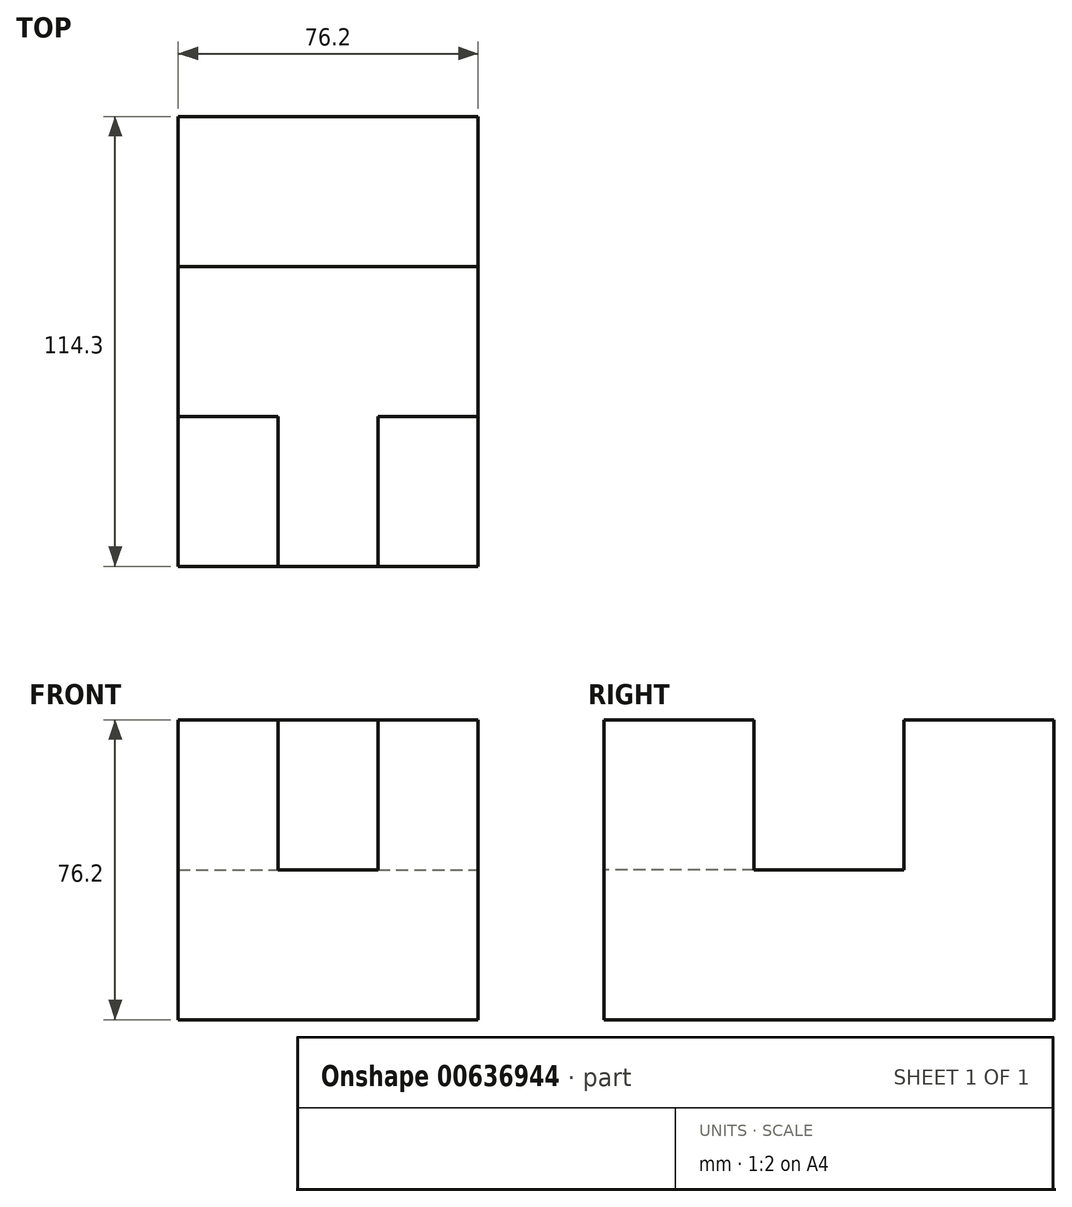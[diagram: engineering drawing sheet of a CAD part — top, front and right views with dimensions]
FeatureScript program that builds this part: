
annotation { "Feature Type Name" : "Feature", "Feature Type Description" : "" }
export const myFeature = defineFeature(function(context is Context, id is Id, definition is map)
    precondition{}
    {
        {
            var Q0;
            Q0=qCreatedBy(makeId("Top.planeOp"),FACE);
            var sketch = newSketch(context, id + "F0", { "sketchPlane" : qUnion([Q0])});
            skLineSegment(sketch, "E0.bottom", {"start": v(-37.87, 64.68) * mm, "end": v(38.33, 64.68) * mm});
            skLineSegment(sketch, "E0.top", {"start": v(-37.87, -49.62) * mm, "end": v(38.33, -49.62) * mm});
            skLineSegment(sketch, "E0.left", {"start": v(-37.87, 64.68) * mm, "end": v(-37.87, -49.62) * mm});
            skLineSegment(sketch, "E0.right", {"start": v(38.33, 64.68) * mm, "end": v(38.33, -49.62) * mm});
            skLineSegment(sketch, "E1.left", {"start": v(-37.87, 64.68) * mm, "end": v(-37.87, 26.58) * mm});
            skLineSegment(sketch, "E1.right", {"start": v(38.33, 64.68) * mm, "end": v(38.33, 26.58) * mm});
            skLineSegment(sketch, "E2.bottom", {"start": v(-37.87, -49.62) * mm, "end": v(-12.47, -49.62) * mm});
            skLineSegment(sketch, "E2.left", {"start": v(-37.87, -49.62) * mm, "end": v(-37.87, -11.52) * mm});
            skLineSegment(sketch, "E3.bottom", {"start": v(38.33, -49.62) * mm, "end": v(12.93, -49.62) * mm});
            skLineSegment(sketch, "E3.left", {"start": v(38.33, -49.62) * mm, "end": v(38.33, -11.52) * mm});
            skPoint(sketch, "E2.right.end.orphan", {"position": v(-12.47, -11.52) * mm});
            skPoint(sketch, "E3.right.end.orphan", {"position": v(12.93, -11.52) * mm});
            skSolve(sketch);
        }
        {
            var Q0;
            Q0=makeQuery(id+"F0.imprint","IMPRINT",FACE,{"disambiguationData":[TD([[makeQuery(id+"F0.imprint","IMPRINT",EDGE,{"derivedFrom":sQuery(id+"F0.wireOp",EDGE,"E0.top")}),1.0]])]});
            var Q1;
            Q1=makeQuery(id+"F0.imprint","IMPRINT",FACE,{"disambiguationData":[TD([[makeQuery(id+"F0.imprint","IMPRINT",EDGE,{"derivedFrom":sQuery(id+"F0.wireOp",EDGE,"E2.bottom")}),1.0]])]});
            var Q2;
            Q2=makeQuery(id+"F0.imprint","IMPRINT",FACE,{"disambiguationData":[TD([[makeQuery(id+"F0.imprint","IMPRINT",EDGE,{"derivedFrom":sQuery(id+"F0.wireOp",EDGE,"E3.bottom")}),-1.0]])]});
            var Q3;
            Q3=makeQuery(id+"F0.imprint","IMPRINT",FACE,{"disambiguationData":[TD([[makeQuery(id+"F0.imprint","IMPRINT",EDGE,{"derivedFrom":sQuery(id+"F0.wireOp",EDGE,"E0.bottom")}),-1.0]])]});
            extrude(context, id + "F1", {"entities" : qUnion([Q0, Q1, Q2, Q3]), "depth" : 76.2 * mm, "offsetDistance" : 25.4 * mm});
        }
        {
            var Q0;
            Q0=makeQuery(id+"F1.opExtrude","CAP_FACE",FACE,{"disambiguationData":[OSD([sQuery(id+"F0.wireOp",EDGE,"E0.top"),sQuery(id+"F0.wireOp",EDGE,"E0.left"),sQuery(id+"F0.wireOp",EDGE,"E0.right"),sQuery(id+"F0.wireOp",EDGE,"E0.bottom"),sQuery(id+"F0.wireOp",EDGE,"E1.left"),sQuery(id+"F0.wireOp",EDGE,"E1.right"),sQuery(id+"F0.wireOp",EDGE,"E2.bottom"),sQuery(id+"F0.wireOp",EDGE,"E2.left"),sQuery(id+"F0.wireOp",EDGE,"E3.bottom"),sQuery(id+"F0.wireOp",EDGE,"E3.left")])],"isStart":false});
            var sketch = newSketch(context, id + "F2", { "sketchPlane" : qUnion([Q0])});
            skLineSegment(sketch, "E4.bottom", {"start": v(-37.87, 64.68) * mm, "end": v(38.33, 64.68) * mm});
            skLineSegment(sketch, "E4.top", {"start": v(-37.87, 26.58) * mm, "end": v(38.33, 26.58) * mm});
            skLineSegment(sketch, "E4.left", {"start": v(-37.87, 64.68) * mm, "end": v(-37.87, 26.58) * mm});
            skLineSegment(sketch, "E4.right", {"start": v(38.33, 64.68) * mm, "end": v(38.33, 26.58) * mm});
            skLineSegment(sketch, "E5.top", {"start": v(-37.87, -11.52) * mm, "end": v(-12.47, -11.52) * mm});
            skLineSegment(sketch, "E5.left", {"start": v(-37.87, 26.58) * mm, "end": v(-37.87, -11.52) * mm});
            skLineSegment(sketch, "E5.right", {"start": v(38.33, 26.58) * mm, "end": v(38.33, -11.52) * mm});
            skLineSegment(sketch, "E6.top", {"start": v(-12.47, -49.62) * mm, "end": v(12.93, -49.62) * mm});
            skLineSegment(sketch, "E6.left", {"start": v(-12.47, -11.52) * mm, "end": v(-12.47, -49.62) * mm});
            skLineSegment(sketch, "E6.right", {"start": v(12.93, -11.52) * mm, "end": v(12.93, -49.62) * mm});
            skLineSegment(sketch, "E7.trimOffspring", {"start": v(12.93, -11.52) * mm, "end": v(38.33, -11.52) * mm});
            skSolve(sketch);
        }
        {
            var Q0;
            Q0=makeQuery(id+"F2.imprint","IMPRINT",FACE,{"disambiguationData":[TD([[makeQuery(id+"F2.imprint","IMPRINT",EDGE,{"derivedFrom":sQuery(id+"F2.wireOp",EDGE,"E4.top")}),-1.0]])]});
            extrude(context, id + "F3", {"entities" : qUnion([Q0]), "operationType" : NewBodyOperationType.REMOVE, "oppositeDirection" : true, "depth" : 38.1 * mm, "offsetDistance" : 25.4 * mm});
        }
    });
